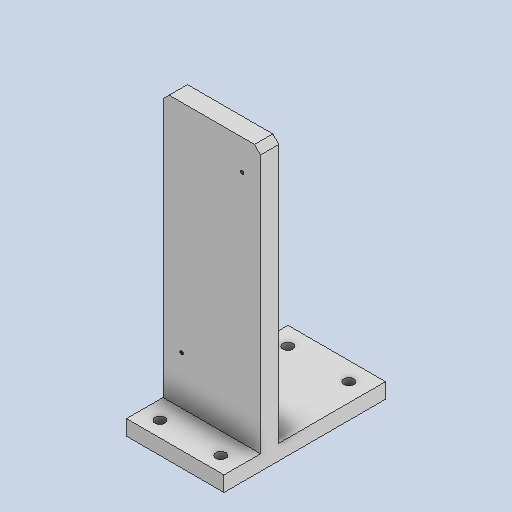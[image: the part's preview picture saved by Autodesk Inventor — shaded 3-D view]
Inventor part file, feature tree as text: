
AUTODESK INVENTOR PART (.ipt)
format: ipt  version: 2024.2 (Build 282272000, 272)  size: 246,784 bytes
history: native  units: mm
features: extrude x7, hole x4, sketch x3, chamfer x1
ambient origin geometry x8: Origin, YZ Plane, XZ Plane, XY Plane, X Axis, Y Axis, Z Axis, Center Point
bodies: Solid1 (feature_tree)
feature tree (15):
  extrude  "Extrusion1"  TaperAngle=45.0deg  [1 undecoded]
  sketch  "Sketch5"  dims[d3=0.0mm d33=45.0deg]
  extrude  "Extrusion3"  Depth=5.0mm
  extrude  "Extrusion4"  TaperAngle=45.0deg  [1 undecoded]
  hole  "Hole3"  [1 undecoded]
  hole  "Hole4"  [1 undecoded]
  chamfer  "Chamfer1"  Distance=5.0mm
  hole  "Hole5"  [1 undecoded]
  extrude  "Extrusion6"  Depth=2.0mm
  extrude  "Extrusion7"  Depth=2.0mm
  hole  "Hole6"  [1 undecoded]
  extrude  "Extrusion8"  Depth=3.0mm TaperAngle=0.0deg
  extrude  "Extrusion9"  TaperAngle=0.0deg  [1 undecoded]
  sketch  "Sketch8"  dims[d35=0.0mm d36=5.0mm]
  sketch  "Sketch14"  dims[d37=5.0mm d38=45.0deg d39=9.999938mm d42=0.0mm d43=5.0mm d44=2.0mm d45=2.0mm d46=2.0mm d47=2.0mm d48=3.0mm d49=0.0mm d52=0.0mm d53=4.496mm d54=6.0mm d55=7.938mm d56=4.166mm d57=14.3117mm d58=8.0mm d59=20.594885mm d60=6.0mm d61=6.0mm d62=6.0mm d63=0.0mm d64=45.0deg d65=0.0mm d66=5.0mm d67=5.0mm d68=45.0deg d69=9.999938mm d70=0.0mm d71=5.0mm d72=2.0mm d73=2.0mm d74=2.0mm d75=2.0mm d76=2.4mm d77=4.0mm d78=4.4mm d79=2.0mm d80=90.0deg d81=5.0mm d82=20.594885mm d83=2.0mm d84=2.0mm d85=45.0deg d90=9.912mm d91=9.912mm d92=3.5mm d93=3.5mm d94=4.496mm d95=4.0mm d96=8.433mm d97=2.0mm d98=14.3117mm d99=5.0mm d100=20.594885mm d103=18.0mm d104=0.0mm d105=5.0mm d106=0.0mm d107=32.0mm d109=3.302mm d110=8.0mm d111=4.0mm d112=2.0mm d113=90.0deg d114=8.0mm d115=0.0mm d116=10.0mm d117=10.0mm d118=32.0mm d119=32.0mm d120=10.0mm d121=10.0mm d122=20.0mm d123=10.0mm d124=10.0mm d125=35.0mm d127=6.0mm d128=18.0mm d129=10.0mm d130=0.0mm d131=2.0mm d132=3.0mm d133=0.0mm]
note: 7 required parameter values undecoded (feature->parameter linkage not recoverable at this tier; creation-order binding heuristic only, values carry confidence <= 0.55)
